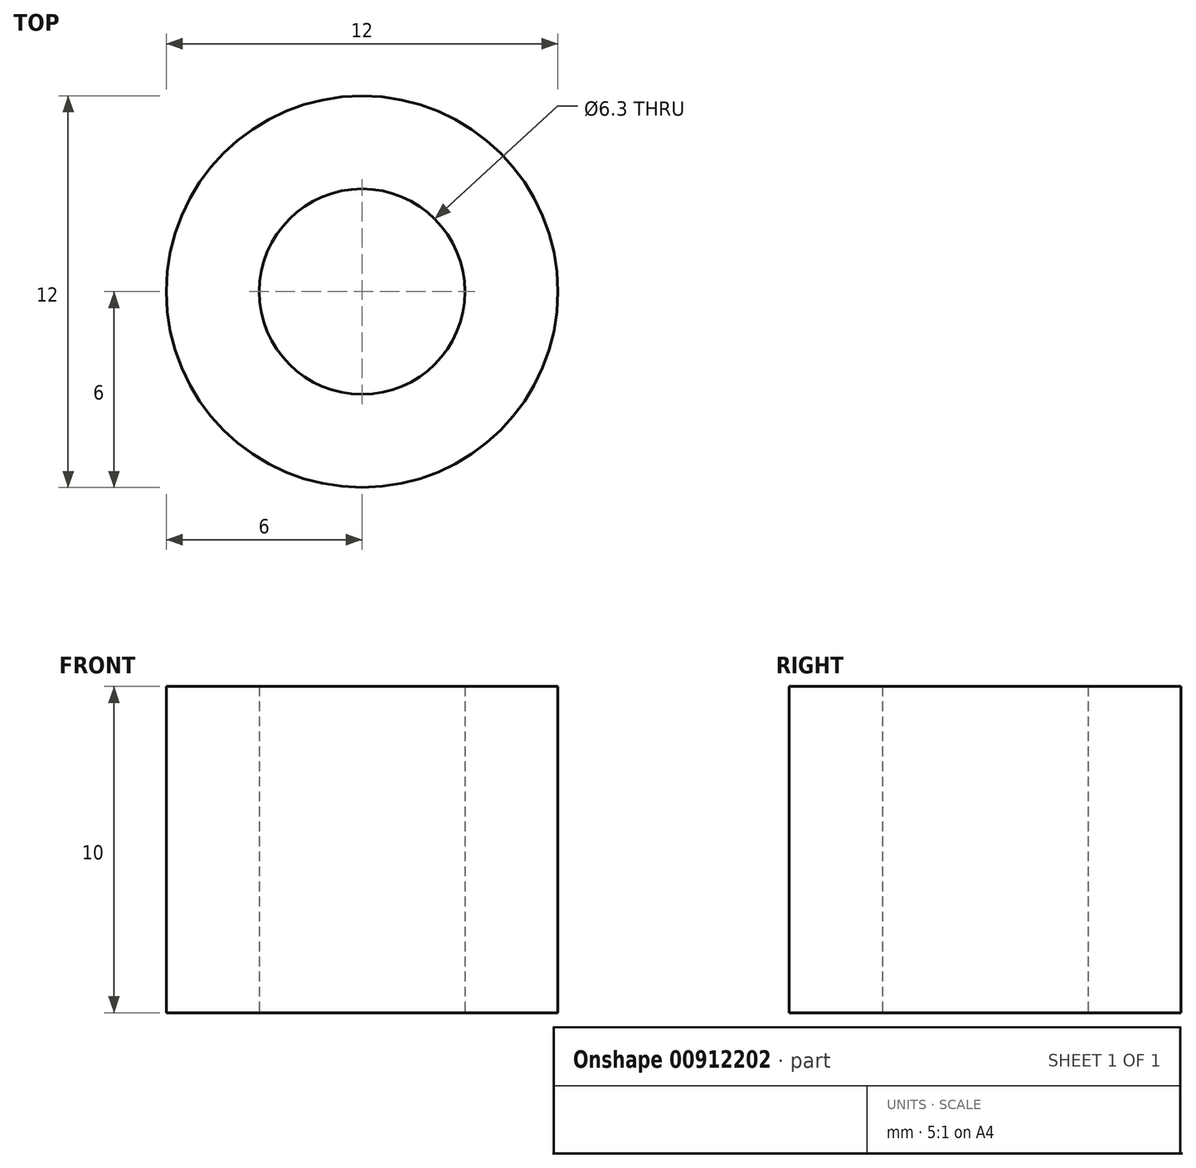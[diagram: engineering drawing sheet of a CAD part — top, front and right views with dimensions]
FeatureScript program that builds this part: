
annotation { "Feature Type Name" : "Feature", "Feature Type Description" : "" }
export const myFeature = defineFeature(function(context is Context, id is Id, definition is map)
    precondition{}
    {
        {
            var Q0;
            Q0=qCreatedBy(makeId("Top.planeOp"),FACE);
            var sketch = newSketch(context, id + "F0", { "sketchPlane" : qUnion([Q0])});
            skCircle(sketch, "E0", {"center": v(0, 0) * mm, "radius": 3.15 * mm});
            skCircle(sketch, "E1", {"center": v(0, 0) * mm, "radius": 6 * mm});
            skSolve(sketch);
        }
        {
            var Q0;
            Q0=makeQuery(id+"F0.imprint","IMPRINT",FACE,{"disambiguationData":[TD([[makeQuery(id+"F0.imprint","IMPRINT",EDGE,{"derivedFrom":sQuery(id+"F0.wireOp",EDGE,"E0")}),-1.0]])]});
            extrude(context, id + "F1", {"entities" : qUnion([Q0]), "depth" : 10 * mm, "offsetDistance" : 25 * mm});
        }
    });
